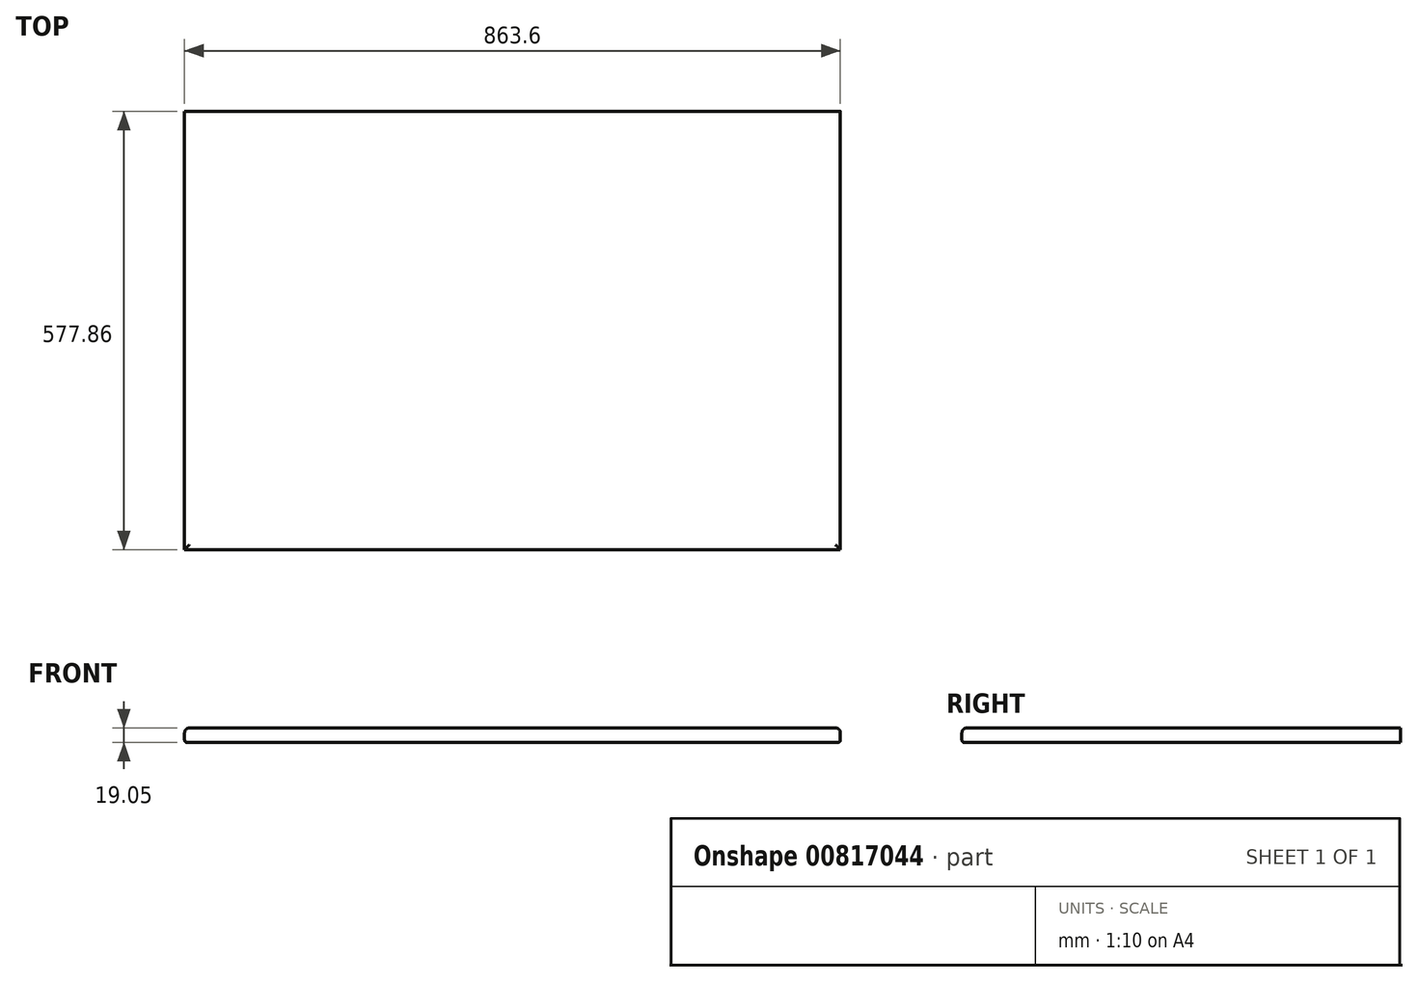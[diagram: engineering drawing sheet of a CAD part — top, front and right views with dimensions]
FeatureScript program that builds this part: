
annotation { "Feature Type Name" : "Feature", "Feature Type Description" : "" }
export const myFeature = defineFeature(function(context is Context, id is Id, definition is map)
    precondition{}
    {
        {
            var Q0;
            Q0=qCreatedBy(makeId("Top.planeOp"),FACE);
            var sketch = newSketch(context, id + "F0", { "sketchPlane" : qUnion([Q0])});
            skLineSegment(sketch, "E0.bottom", {"start": v(431.8, 288.93) * mm, "end": v(-431.8, 288.93) * mm});
            skLineSegment(sketch, "E0.top", {"start": v(431.8, -288.93) * mm, "end": v(-431.8, -288.93) * mm});
            skLineSegment(sketch, "E0.left", {"start": v(431.8, 288.93) * mm, "end": v(431.8, -288.93) * mm});
            skLineSegment(sketch, "E0.right", {"start": v(-431.8, 288.93) * mm, "end": v(-431.8, -288.93) * mm});
            skPoint(sketch, "E0.middle", {"position": v(0, 0) * mm});
            skSolve(sketch);
        }
        {
            var Q0;
            Q0 = qSketchRegion(id + "F0", true);
            extrude(context, id + "F1", {"entities" : qUnion([Q0]), "depth" : 19.05 * mm, "offsetDistance" : 25.4 * mm});
        }
        {
            var Q0;
            Q0=makeQuery(id+"F1.opExtrude","CAP_EDGE",EDGE,{"disambiguationData":[OSD([sQuery(id+"F0.wireOp",EDGE,"E0.right")])],"isStart":false});
            var Q1;
            Q1=makeQuery(id+"F1.opExtrude","CAP_EDGE",EDGE,{"disambiguationData":[OSD([sQuery(id+"F0.wireOp",EDGE,"E0.top")])],"isStart":false});
            var Q2;
            Q2=makeQuery(id+"F1.opExtrude","CAP_EDGE",EDGE,{"disambiguationData":[OSD([sQuery(id+"F0.wireOp",EDGE,"E0.left")])],"isStart":false});
            fillet(context, id + "F2", {"entities" : qUnion([Q0, Q1, Q2]), "radius" : 6.35 * mm, "tangentPropagation" : true, "allowEdgeOverflow" : false});
        }
        {
            var Q0;
            Q0=makeQuery(id+"F1.opExtrude","CAP_EDGE",EDGE,{"disambiguationData":[OSD([sQuery(id+"F0.wireOp",EDGE,"E0.right")])],"isStart":true});
            var Q1;
            Q1=makeQuery(id+"F1.opExtrude","CAP_EDGE",EDGE,{"disambiguationData":[OSD([sQuery(id+"F0.wireOp",EDGE,"E0.top")])],"isStart":true});
            var Q2;
            Q2=makeQuery(id+"F1.opExtrude","CAP_EDGE",EDGE,{"disambiguationData":[OSD([sQuery(id+"F0.wireOp",EDGE,"E0.left")])],"isStart":true});
            fillet(context, id + "F3", {"entities" : qUnion([Q0, Q1, Q2]), "radius" : 3.17 * mm, "tangentPropagation" : true, "allowEdgeOverflow" : false});
        }
    });
